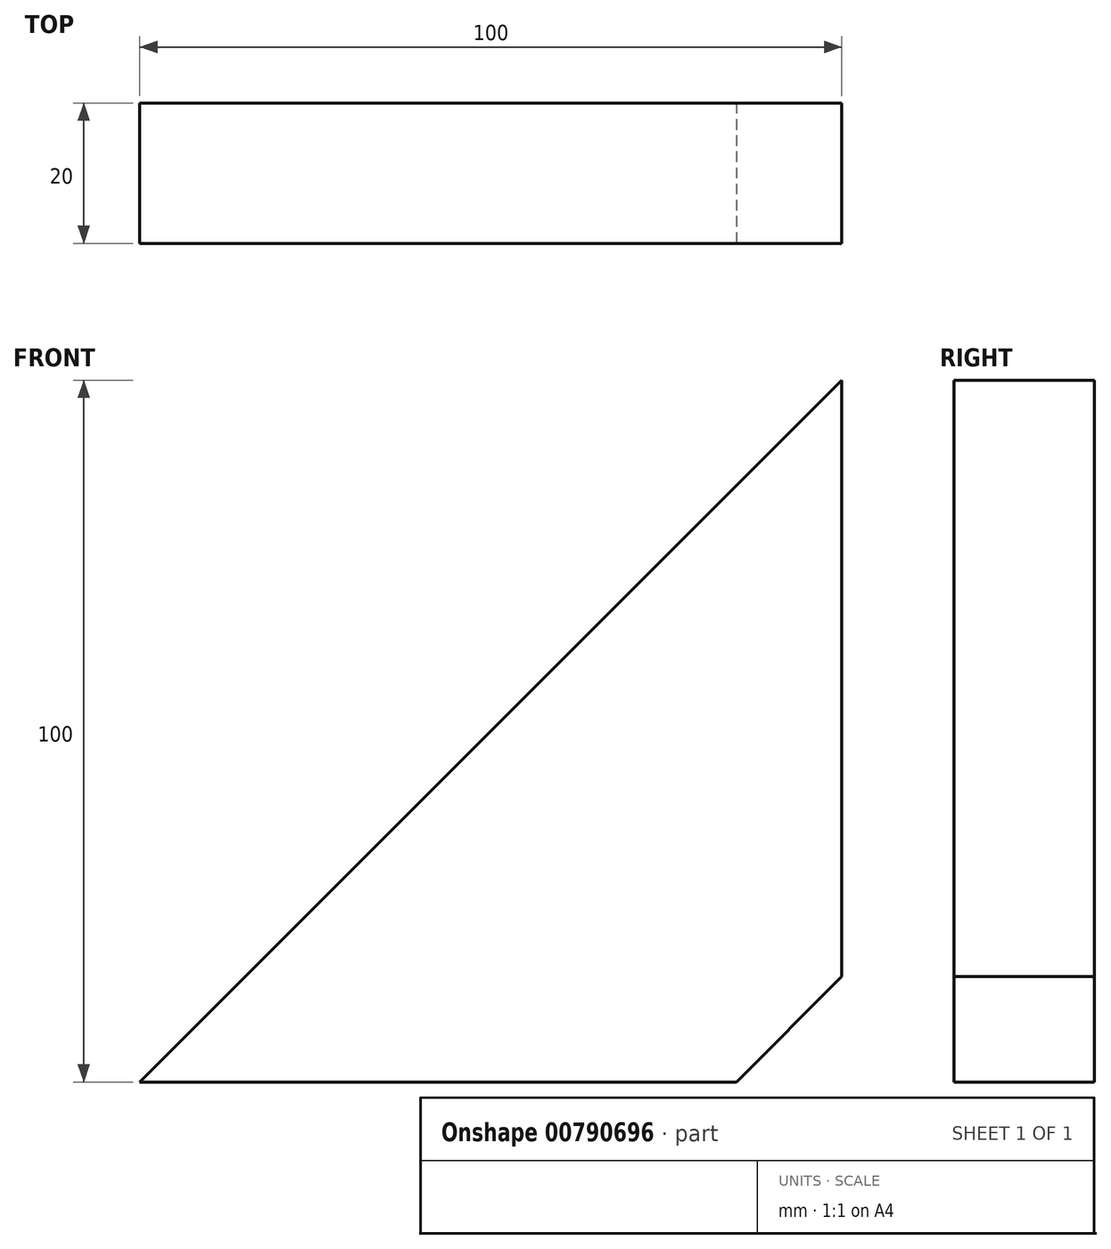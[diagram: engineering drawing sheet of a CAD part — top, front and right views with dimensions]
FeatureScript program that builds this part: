
annotation { "Feature Type Name" : "Feature", "Feature Type Description" : "" }
export const myFeature = defineFeature(function(context is Context, id is Id, definition is map)
    precondition{}
    {
        {
            var Q0;
            Q0=qCreatedBy(makeId("Front.planeOp"),FACE);
            var sketch = newSketch(context, id + "F0", { "sketchPlane" : qUnion([Q0])});
            skLineSegment(sketch, "E0", {"start": v(0, 0) * mm, "end": v(-100, 0) * mm});
            skLineSegment(sketch, "E1", {"start": v(0, 0) * mm, "end": v(0, 100) * mm});
            skLineSegment(sketch, "E2", {"start": v(0, 100) * mm, "end": v(-100, 0) * mm});
            skSolve(sketch);
        }
        {
            var Q0;
            Q0=makeQuery(id+"F0.imprint","IMPRINT",FACE,{"disambiguationData":[TD([[makeQuery(id+"F0.imprint","IMPRINT",EDGE,{"derivedFrom":sQuery(id+"F0.wireOp",EDGE,"E0")}),-1.0]])]});
            extrude(context, id + "F1", {"entities" : qUnion([Q0]), "depth" : 20 * mm, "offsetDistance" : 25 * mm});
        }
        {
            var Q0;
            Q0=makeQuery(id+"F1.opExtrude","SWEPT_EDGE",EDGE,{"disambiguationData":[OSD([sQuery(id+"F0.wireOp",EDGE,"E0"),sQuery(id+"F0.wireOp",EDGE,"E1")])]});
            chamfer(context, id + "F2", {"entities" : qUnion([Q0]), "width" : 15 * mm, "tangentPropagation" : true});
        }
    });
